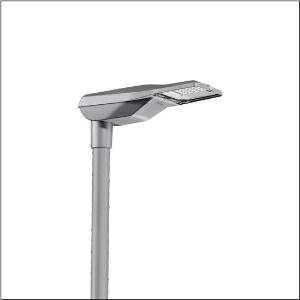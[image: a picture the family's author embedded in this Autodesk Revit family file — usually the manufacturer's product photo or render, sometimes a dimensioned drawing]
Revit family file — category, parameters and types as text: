
# Revit family: streetlight_sl_21_iq_micro___stw1_0a_5xe1e31d08cb_0f3c
name_source: partatom
category: Lighting Fixtures
units: mm (PartAtom-declared; Revit-internal decimal feet)

## family parameters
Cut with Voids When Loaded = No
Host = Face
Light Source = No
Part Type = Normal
Room Calculation Point = No
Round Connector Dimension = Use Diameter
Shared = No

## types (1)
- --- (1 x LED, 2870 lm, 19.4 W, 3000K)
    Apparent Load = 19 VA
    CIE Flux Codes = 38 75 98 100 100
    Color Rendering = 70
    Color Temperature = 3000K
    Default Elevation = 1800 mm
    Description = Streetlight SL 21 iQ micro, mast luminaire, primary light control with lens, of PMMA, primary optical cover: cover, of toughened safety glass, transparent, light distribution: STW1.0a, light emission: direct distribution, primary light characteristic: asymmetric, installation type: post-top, side-entry, LED, High Power LED, rated luminous flux: 2.870lm, luminous efficacy: 148lm/W, light colour: 730, colour temperature: 3000K, control: Auto-Match, Temp-Guard, Lumen-Switch, Night-Set, Smart-Wire, Light-Fading, Desk-Remote (wireless, voltage-free reading and setting of iQ features in the workshop via application-optimized NFC function/RFID function), optimised constant luminous flux control (CLO 2.0), pre-setting: linear dimming characteristic, mains connection: 220..240V, AC, 50/60Hz, start of lifetime: 19W, end of service life: 20W, reduction: 10W, luminaire housing, of diecast aluminium, powder-coated, Siteco® metallic grey (DB 702S), corrosivity category C5 mid according to DIN EN ISO 12944, please order mast flange separately, inclination adjustable: 0°, 5°, 10°, 15°, sealing non-destructively replaceable, multi-level sealing system, length: 528mm, width: 235mm, height: 110mm, mast flange for spigot size: 42mm (side-entry): 5XC10008XM4, 60/48mm (side-entry/post-top): 5XC10108XM2, 76/60mm (side-entry/post-top): 5XC10108XM1, protection rating (complete): IP66, insulation class (complete): insulation class II (safety insulation), certification: CE, ENEC, ENEC+, VDE, impact resistance: IK09, permissible operating ambient temperature for outdoor applications: -40..+50°C, standard-compliant lighting for roads and squares, packaging unit: 1 piece

Light Distribution: STW1.0a
    Height = 110 mm
    Lamp = 1 x LED
    Lamp Light Flux = 2870 lm
    Lamp Power = 19.4 W
    Lamp count = 1
    Length = 528 mm
    Luminous efficacy = 148 lm/W
    Manufacturer = Siteco
    ModVariant = No
    Model = 5XE1E31D08CB
    Number of Poles = 1
    OnlyDefault = Yes
    Power Factor = 1
    Product Name = Streetlight SL 21 iQ micro | STW1.0a
    Product group = mast luminaire | pylon top
    ProductGroupID = 6100
    Protection Class = Protection class II
    Protection Degree = IP 66
    RLX_Detail_Level = 1
    RLX_Emergency_Light_Flux = 0 lm
    RLX_Emergency_Type = 0
    RLX_Emergency_Type_DB = No
    RlxData = <blob elided: 98409 chars, md5=e2ac34ef>
    Socket = socket
    Standby Power = 0 W
    System Light Flux = 2870 lm
    System Power = 19 W
    Type Comments = factory setting: luminous flux: 100 % | dim-lin: 254 | 387 mA
    Type Image = l_1006881.jpg
    URL = http://relux.com
    VarID = @adj_108699
    Voltage = 0 V
    Weight = 0.00 kg
    Width = 235 mm

## geometry (parser evidence)
native form markers: Blend x4, Sweep x11
no freeform markers — native parametric forms only
